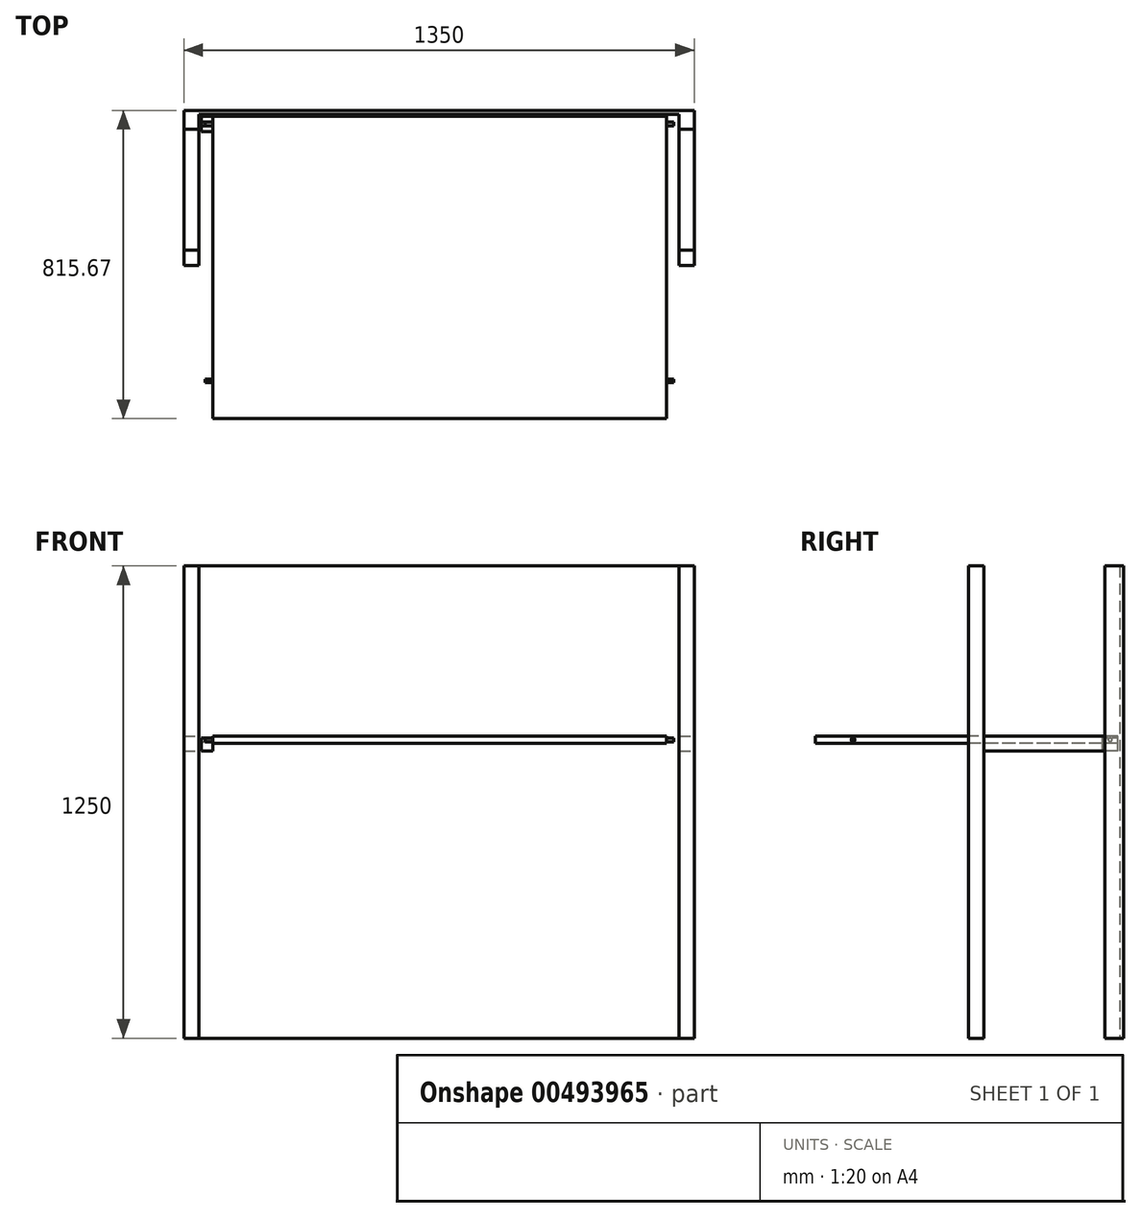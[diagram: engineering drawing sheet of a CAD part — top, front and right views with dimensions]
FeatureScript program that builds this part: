
annotation { "Feature Type Name" : "Feature", "Feature Type Description" : "" }
export const myFeature = defineFeature(function(context is Context, id is Id, definition is map)
    precondition{}
    {
        {
            var Q0;
            Q0=qCreatedBy(makeId("Top.planeOp"),FACE);
            var sketch = newSketch(context, id + "F0", { "sketchPlane" : qUnion([Q0])});
            skLineSegment(sketch, "E0", {"start": v(-668.2, -32.31) * mm, "end": v(601.8, -32.31) * mm});
            skLineSegment(sketch, "E1", {"start": v(-668.2, -32.31) * mm, "end": v(-668.2, -72.31) * mm});
            skLineSegment(sketch, "E2", {"start": v(-708.2, -72.31) * mm, "end": v(-708.2, -392.31) * mm});
            skLineSegment(sketch, "E3", {"start": v(-668.2, -392.31) * mm, "end": v(-668.2, -432.31) * mm});
            skLineSegment(sketch, "E4", {"start": v(-668.2, -432.31) * mm, "end": v(-708.2, -432.31) * mm});
            skLineSegment(sketch, "E5", {"start": v(-708.2, -432.31) * mm, "end": v(-708.2, -392.31) * mm});
            skLineSegment(sketch, "E6", {"start": v(-668.2, -72.31) * mm, "end": v(-668.2, -392.31) * mm});
            skLineSegment(sketch, "E7", {"start": v(-708.2, -72.31) * mm, "end": v(-708.2, -32.31) * mm});
            skLineSegment(sketch, "E8", {"start": v(-708.2, -32.31) * mm, "end": v(-708.2, -22.31) * mm});
            skLineSegment(sketch, "E9", {"start": v(-708.2, -22.31) * mm, "end": v(601.8, -22.31) * mm});
            skLineSegment(sketch, "E10", {"start": v(601.8, -22.31) * mm, "end": v(641.8, -22.31) * mm});
            skLineSegment(sketch, "E11", {"start": v(641.8, -22.31) * mm, "end": v(641.8, -432.31) * mm});
            skLineSegment(sketch, "E12", {"start": v(641.8, -432.31) * mm, "end": v(601.8, -432.31) * mm});
            skLineSegment(sketch, "E13", {"start": v(601.8, -432.31) * mm, "end": v(601.8, -32.31) * mm});
            skLineSegment(sketch, "E14", {"start": v(-708.2, -72.31) * mm, "end": v(-668.2, -72.31) * mm});
            skLineSegment(sketch, "E15", {"start": v(-708.2, -392.31) * mm, "end": v(-668.2, -392.31) * mm});
            skLineSegment(sketch, "E16", {"start": v(601.8, -392.31) * mm, "end": v(641.8, -392.31) * mm});
            skLineSegment(sketch, "E17", {"start": v(601.8, -72.31) * mm, "end": v(641.8, -72.31) * mm});
            skSolve(sketch);
        }
        {
            var Q0;
            Q0=makeQuery(id+"F0.imprint","IMPRINT",FACE,{"disambiguationData":[TD([[makeQuery(id+"F0.imprint","IMPRINT",EDGE,{"derivedFrom":sQuery(id+"F0.wireOp",EDGE,"E3")}),-1.0]])]});
            var Q1;
            {var subQ0=sQuery(id+"F0.wireOp",EDGE,"E0");Q1=makeQuery(id+"F0.imprint","IMPRINT",FACE,{"disambiguationData":[TD([[makeQuery(id+"F0.imprint","IMPRINT",EDGE,{"derivedFrom":subQ0}),1.0]])]});}
            var Q2;
            {var subQ0=sQuery(id+"F0.wireOp",EDGE,"E12");Q2=makeQuery(id+"F0.imprint","IMPRINT",FACE,{"disambiguationData":[TD([[makeQuery(id+"F0.imprint","IMPRINT",EDGE,{"derivedFrom":subQ0}),-1.0]])]});}
            extrude(context, id + "F1", {"entities" : qUnion([Q0, Q1, Q2]), "depth" : 1250 * mm, "offsetDistance" : 25.4 * mm});
        }
        {
            var Q0;
            Q0=makeQuery(id+"F1.opExtrude","SWEPT_FACE",FACE,{"disambiguationData":[OSD([sQuery(id+"F0.wireOp",EDGE,"E3")])]});
            var sketch = newSketch(context, id + "F2", { "sketchPlane" : qUnion([Q0])});
            skLineSegment(sketch, "E18.bottom", {"start": v(-392.31, 760) * mm, "end": v(-72.31, 760) * mm});
            skLineSegment(sketch, "E18.top", {"start": v(-392.31, 800) * mm, "end": v(-72.31, 800) * mm});
            skLineSegment(sketch, "E18.left", {"start": v(-392.31, 760) * mm, "end": v(-392.31, 800) * mm});
            skLineSegment(sketch, "E18.right", {"start": v(-72.31, 760) * mm, "end": v(-72.31, 800) * mm});
            skSolve(sketch);
        }
        {
            var Q0;
            Q0=makeQuery(id+"F2.imprint","IMPRINT",FACE,{"disambiguationData":[TD([[makeQuery(id+"F2.imprint","IMPRINT",EDGE,{"derivedFrom":sQuery(id+"F2.wireOp",EDGE,"E18.bottom")}),1.0]])]});
            extrude(context, id + "F3", {"entities" : qUnion([Q0]), "oppositeDirection" : true, "depth" : 40 * mm, "offsetDistance" : 25.4 * mm});
        }
        {
            var Q0;
            {var subQ0=sQuery(id+"F0.wireOp",EDGE,"E11");Q0=makeQuery(id+"F1.opExtrude","SWEPT_FACE",FACE,{"disambiguationData":[OSD([subQ0]),TDD([makeQuery(id+"F0.imprint","IMPRINT",EDGE,{"disambiguationData":[TD([[makeQuery(id+"F0.imprint","INTERSECT",VERTEX,{"derivedFrom":[sQuery(id+"F0.wireOp",EDGE,"E10"),subQ0]}),-1.0]])],"derivedFrom":subQ0})])]});}
            var sketch = newSketch(context, id + "F4", { "sketchPlane" : qUnion([Q0])});
            skLineSegment(sketch, "E19.bottom", {"start": v(-392.31, 760) * mm, "end": v(-72.31, 760) * mm});
            skLineSegment(sketch, "E19.top", {"start": v(-392.31, 800) * mm, "end": v(-72.31, 800) * mm});
            skLineSegment(sketch, "E19.left", {"start": v(-392.31, 760) * mm, "end": v(-392.31, 800) * mm});
            skLineSegment(sketch, "E19.right", {"start": v(-72.31, 760) * mm, "end": v(-72.31, 800) * mm});
            skSolve(sketch);
        }
        {
            var Q0;
            Q0=makeQuery(id+"F4.imprint","IMPRINT",FACE,{"disambiguationData":[TD([[makeQuery(id+"F4.imprint","IMPRINT",EDGE,{"derivedFrom":sQuery(id+"F4.wireOp",EDGE,"E19.bottom")}),1.0]])]});
            extrude(context, id + "F5", {"entities" : qUnion([Q0]), "oppositeDirection" : true, "depth" : 40 * mm, "offsetDistance" : 25.4 * mm});
        }
        {
            var Q0;
            Q0=makeQuery(id+"F5.opExtrude","SWEPT_FACE",FACE,{"disambiguationData":[OSD([sQuery(id+"F4.wireOp",EDGE,"E19.top")])]});
            var sketch = newSketch(context, id + "F6", { "sketchPlane" : qUnion([Q0])});
            skLineSegment(sketch, "E20.bottom", {"start": v(-632.23, -37.98) * mm, "end": v(567.77, -37.98) * mm});
            skLineSegment(sketch, "E20.top", {"start": v(-632.23, -837.98) * mm, "end": v(567.77, -837.98) * mm});
            skLineSegment(sketch, "E20.left", {"start": v(-632.23, -37.98) * mm, "end": v(-632.23, -837.98) * mm});
            skLineSegment(sketch, "E20.right", {"start": v(567.77, -37.98) * mm, "end": v(567.77, -837.98) * mm});
            skSolve(sketch);
        }
        {
            var Q0;
            Q0 = qSketchRegion(id + "F6", true);
            extrude(context, id + "F7", {"entities" : qUnion([Q0]), "oppositeDirection" : true, "depth" : 20 * mm, "offsetDistance" : 25.4 * mm});
        }
        {
            var Q0;
            Q0=makeQuery(id+"F7.opExtrude","SWEPT_FACE",FACE,{"disambiguationData":[OSD([sQuery(id+"F6.wireOp",EDGE,"E20.left")])]});
            var sketch = newSketch(context, id + "F8", { "sketchPlane" : qUnion([Q0])});
            skCircle(sketch, "E21", {"center": v(737.98, 790) * mm, "radius": 5 * mm});
            skPoint(sketch, "E21.centerSnap0", {"position": v(837.98, 790) * mm});
            skCircle(sketch, "E22", {"center": v(57.98, 790) * mm, "radius": 5 * mm});
            skPoint(sketch, "E22.centerSnap0", {"position": v(37.98, 790) * mm});
            skLineSegment(sketch, "E23.bottom", {"start": v(37.98, 780) * mm, "end": v(77.98, 780) * mm});
            skLineSegment(sketch, "E23.top", {"start": v(37.98, 795) * mm, "end": v(77.98, 795) * mm});
            skLineSegment(sketch, "E23.left", {"start": v(37.98, 780) * mm, "end": v(37.98, 795) * mm});
            skLineSegment(sketch, "E23.right", {"start": v(77.98, 780) * mm, "end": v(77.98, 795) * mm});
            skLineSegment(sketch, "E24", {"start": v(52.98, 790) * mm, "end": v(52.98, 795) * mm});
            skLineSegment(sketch, "E25", {"start": v(62.98, 790) * mm, "end": v(62.98, 795) * mm});
            skSolve(sketch);
        }
        {
            var Q0;
            {var subQ0=sQuery(id+"F8.wireOp",EDGE,"E22");var subQ1=makeQuery(id+"F8.imprint","INTERSECT",VERTEX,{"derivedFrom":[subQ0,sQuery(id+"F8.wireOp",EDGE,"E25")]});Q0=makeQuery(id+"F8.imprint","IMPRINT",FACE,{"disambiguationData":[TD([[makeQuery(id+"F8.imprint","IMPRINT",EDGE,{"disambiguationData":[TD([[subQ1,-1.0]])],"derivedFrom":subQ0}),1.0]])]});}
            var Q1;
            Q1=makeQuery(id+"F8.imprint","IMPRINT",FACE,{"disambiguationData":[TD([[makeQuery(id+"F8.imprint","IMPRINT",EDGE,{"derivedFrom":sQuery(id+"F8.wireOp",EDGE,"E21")}),1.0]])]});
            extrude(context, id + "F9", {"entities" : qUnion([Q0, Q1]), "operationType" : NewBodyOperationType.ADD, "depth" : 20 * mm, "offsetDistance" : 25.4 * mm});
        }
        {
            var Q0;
            Q0=makeQuery(id+"F9.opExtrude","CAP_FACE",FACE,{"disambiguationData":[OSD([sQuery(id+"F8.wireOp",EDGE,"E21")])],"isStart":false});
            var Q1;
            Q1=makeQuery(id+"F9.opExtrude","CAP_FACE",FACE,{"disambiguationData":[OSD([sQuery(id+"F8.wireOp",EDGE,"E22")])],"isStart":false});
            extrude(context, id + "F10", {"entities" : qUnion([Q0, Q1]), "operationType" : NewBodyOperationType.ADD, "oppositeDirection" : true, "depth" : 1240 * mm, "offsetDistance" : 25.4 * mm});
        }
        {
            var Q0;
            Q0=makeQuery(id+"F8.imprint","IMPRINT",FACE,{"disambiguationData":[TD([[makeQuery(id+"F8.imprint","IMPRINT",EDGE,{"derivedFrom":sQuery(id+"F8.wireOp",EDGE,"E23.bottom")}),1.0]])]});
            extrude(context, id + "F11", {"entities" : qUnion([Q0]), "depth" : 30 * mm, "offsetDistance" : 25.4 * mm});
        }
        {
            var Q0;
            Q0=makeQuery(id+"F11.opExtrude","SWEPT_FACE",FACE,{"disambiguationData":[OSD([sQuery(id+"F8.wireOp",EDGE,"E23.bottom")])]});
            extrude(context, id + "F12", {"entities" : qUnion([Q0]), "operationType" : NewBodyOperationType.ADD, "depth" : 20 * mm, "offsetDistance" : 25.4 * mm});
        }
    });
